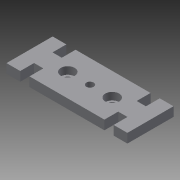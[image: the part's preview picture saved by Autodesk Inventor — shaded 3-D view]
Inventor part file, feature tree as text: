
AUTODESK INVENTOR PART (.ipt)
format: ipt  version: 2015 (Build 190159000, 159)  size: 119,808 bytes
history: native  units: mm
features: extrude x4, sketch x3
ambient origin geometry x8: Origin, YZ Plane, XZ Plane, XY Plane, X Axis, Y Axis, Z Axis, Center Point
bodies: Body1 (feature_tree)
feature tree (7):
  sketch  "Sketch1"  dims[d0=15.0mm d1=15.0mm d2=15.0mm d3=15.0mm d8=15.0mm]
  extrude  "Extrusion2"  Depth=15.0mm
  extrude  "Extrusion3"  Depth=10.0mm TaperAngle=0.0deg
  extrude  "Extrusion6"  Depth=10.0mm
  extrude  "Extrusion7"  Depth=10.0mm TaperAngle=0.0deg
  sketch  "Sketch2"  dims[d9=15.0mm d10=10.0mm d11=0.0mm]
  sketch  "Sketch3"  dims[d15=2.5mm d16=2.5mm d17=10.0mm d18=0.0mm d25=48.2mm d26=10.0mm d27=10.0mm d28=2.0mm d29=0.0mm d30=8.0mm d31=10.0mm d32=0.0mm]
